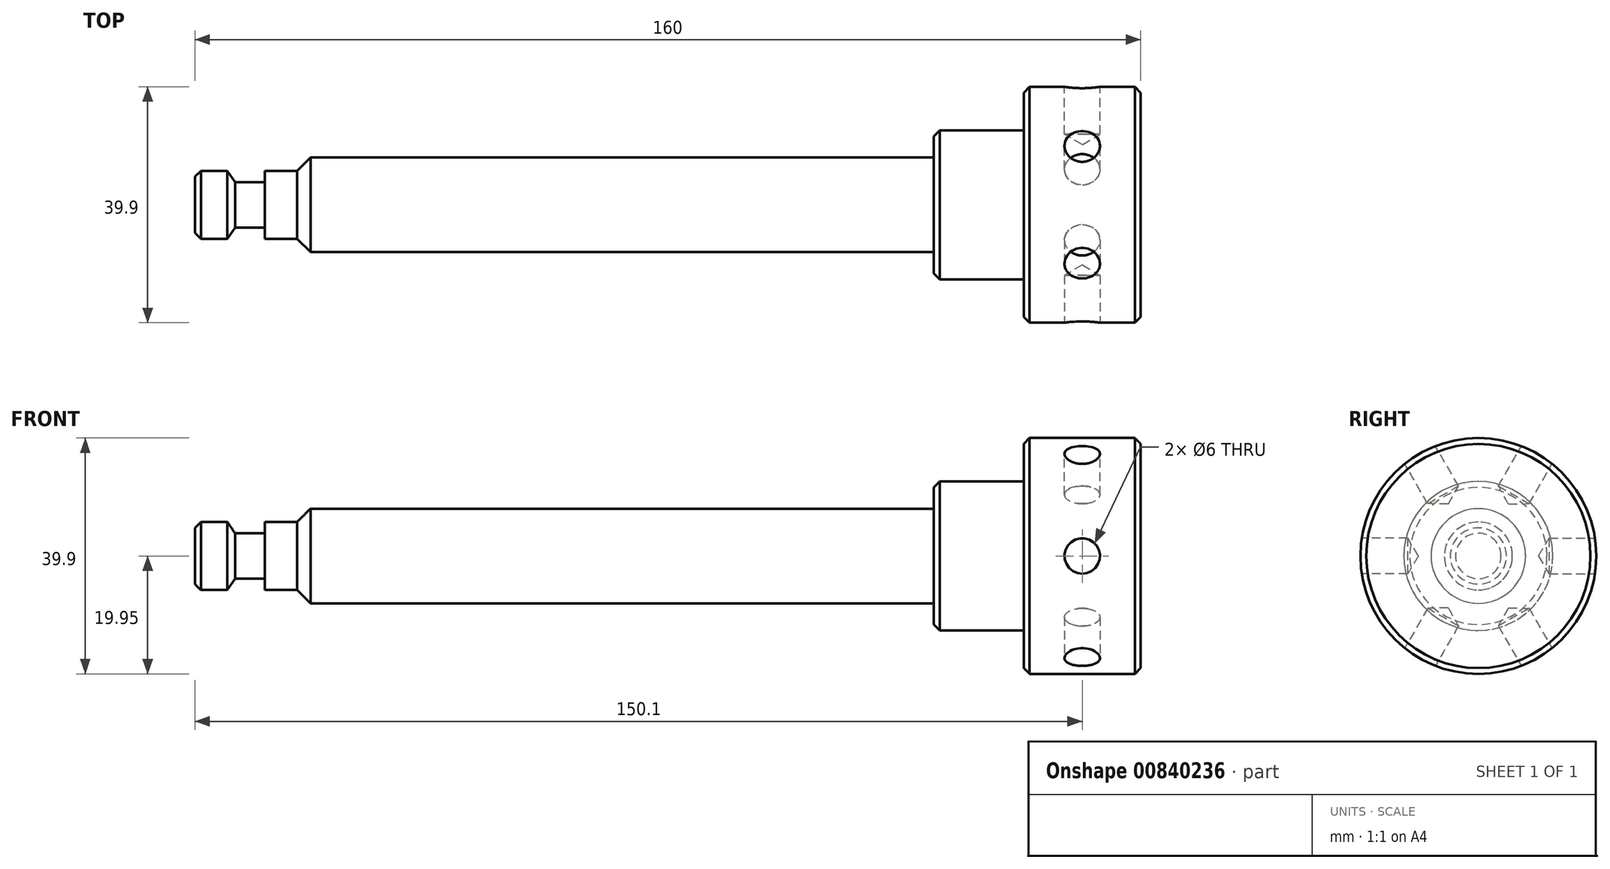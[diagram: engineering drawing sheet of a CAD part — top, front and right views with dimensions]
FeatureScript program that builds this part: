
annotation { "Feature Type Name" : "Feature", "Feature Type Description" : "" }
export const myFeature = defineFeature(function(context is Context, id is Id, definition is map)
    precondition{}
    {
        {
            var Q0;
            Q0=qCreatedBy(makeId("Top.planeOp"),FACE);
            var sketch = newSketch(context, id + "F0", { "sketchPlane" : qUnion([Q0])});
            skLineSegment(sketch, "E0", {"start": v(-0.14, 0) * mm, "end": v(-177.57, 0) * mm, "construction": true});
            skLineSegment(sketch, "E1", {"start": v(0, 0) * mm, "end": v(0, 19.95) * mm});
            skLineSegment(sketch, "E2", {"start": v(0, 19.95) * mm, "end": v(-19.8, 19.95) * mm});
            skLineSegment(sketch, "E3", {"start": v(-19.8, 19.95) * mm, "end": v(-19.8, 12.6) * mm});
            skLineSegment(sketch, "E4", {"start": v(-19.8, 12.6) * mm, "end": v(-35, 12.6) * mm});
            skLineSegment(sketch, "E5", {"start": v(-35, 12.6) * mm, "end": v(-35, 8) * mm});
            skLineSegment(sketch, "E6", {"start": v(-35, 8) * mm, "end": v(-142.7, 8) * mm});
            skLineSegment(sketch, "E7", {"start": v(-142.7, 8) * mm, "end": v(-142.7, 5.75) * mm});
            skLineSegment(sketch, "E8", {"start": v(-142.7, 5.75) * mm, "end": v(-148.2, 5.75) * mm});
            skLineSegment(sketch, "E9", {"start": v(-148.2, 5.75) * mm, "end": v(-148.2, 3.85) * mm});
            skLineSegment(sketch, "E10", {"start": v(-148.2, 3.85) * mm, "end": v(-153.2, 3.85) * mm});
            skLineSegment(sketch, "E11", {"start": v(-153.2, 3.85) * mm, "end": v(-154.5, 5.75) * mm});
            skLineSegment(sketch, "E12", {"start": v(-154.5, 5.75) * mm, "end": v(-160, 5.75) * mm});
            skLineSegment(sketch, "E13", {"start": v(-160, 5.75) * mm, "end": v(-160, 0) * mm});
            skLineSegment(sketch, "E14", {"start": v(-160, 0) * mm, "end": v(0, 0) * mm});
            skSolve(sketch);
        }
        {
            var Q0;
            Q0=makeQuery(id+"F0.imprint","IMPRINT",FACE,{"disambiguationData":[TD([[makeQuery(id+"F0.imprint","IMPRINT",EDGE,{"derivedFrom":sQuery(id+"F0.wireOp",EDGE,"E1")}),1.0]])]});
            var Q1;
            Q1=sQuery(id+"F0.wireOp",EDGE,"E14");
            revolve(context, id + "F1", {"entities" : qUnion([Q0]), "axis" : qUnion([Q1]), "revolveType" : RevolveType.FULL});
        }
        {
            var Q0;
            Q0=makeQuery(id+"F1.opRevolve","SWEPT_EDGE",EDGE,{"disambiguationData":[OSD([sQuery(id+"F0.wireOp",EDGE,"E12"),sQuery(id+"F0.wireOp",EDGE,"E13")])]});
            var Q1;
            Q1=makeQuery(id+"F1.opRevolve","SWEPT_EDGE",EDGE,{"disambiguationData":[OSD([sQuery(id+"F0.wireOp",EDGE,"E1"),sQuery(id+"F0.wireOp",EDGE,"E2")])]});
            var Q2;
            Q2=makeQuery(id+"F1.opRevolve","SWEPT_EDGE",EDGE,{"disambiguationData":[OSD([sQuery(id+"F0.wireOp",EDGE,"E4"),sQuery(id+"F0.wireOp",EDGE,"E5")])]});
            var Q3;
            Q3=makeQuery(id+"F1.opRevolve","SWEPT_EDGE",EDGE,{"disambiguationData":[OSD([sQuery(id+"F0.wireOp",EDGE,"E2"),sQuery(id+"F0.wireOp",EDGE,"E3")])]});
            chamfer(context, id + "F2", {"entities" : qUnion([Q0, Q1, Q2, Q3]), "width" : 1 * mm, "tangentPropagation" : true});
        }
        {
            var Q0;
            Q0=makeQuery(id+"F1.opRevolve","SWEPT_EDGE",EDGE,{"disambiguationData":[OSD([sQuery(id+"F0.wireOp",EDGE,"E6"),sQuery(id+"F0.wireOp",EDGE,"E7")])]});
            chamfer(context, id + "F3", {"entities" : qUnion([Q0]), "width" : 2.25 * mm, "tangentPropagation" : true});
        }
        {
            var Q0;
            Q0=makeQuery(id+"F1.opRevolve","SWEPT_FACE",FACE,{"disambiguationData":[OSD([sQuery(id+"F0.wireOp",EDGE,"E1")])]});
            var sketch = newSketch(context, id + "F4", { "sketchPlane" : qUnion([Q0])});
            skLineSegment(sketch, "E15", {"start": v(0, 0) * mm, "end": v(26.9, 0) * mm, "construction": true});
            skLineSegment(sketch, "E16", {"start": v(19.95, 12.37) * mm, "end": v(19.95, -12.53) * mm, "construction": true});
            skLineSegment(sketch, "E17.1.0", {"start": v(-0.74, 23.46) * mm, "end": v(20.82, 11.01) * mm, "construction": true});
            skLineSegment(sketch, "E17.1.1", {"start": v(0, 0) * mm, "end": v(13.45, 23.3) * mm, "construction": true});
            skLineSegment(sketch, "E17.2.0", {"start": v(-20.69, 11.1) * mm, "end": v(0.87, 23.54) * mm, "construction": true});
            skLineSegment(sketch, "E17.2.1", {"start": v(0, 0) * mm, "end": v(-13.45, 23.3) * mm, "construction": true});
            skLineSegment(sketch, "E17.3.0", {"start": v(-19.95, -12.37) * mm, "end": v(-19.95, 12.53) * mm, "construction": true});
            skLineSegment(sketch, "E17.3.1", {"start": v(0, 0) * mm, "end": v(-26.9, 0) * mm, "construction": true});
            skLineSegment(sketch, "E17.4.0", {"start": v(0.74, -23.46) * mm, "end": v(-20.82, -11.01) * mm, "construction": true});
            skLineSegment(sketch, "E17.4.1", {"start": v(0, 0) * mm, "end": v(-13.45, -23.3) * mm, "construction": true});
            skLineSegment(sketch, "E17.5.0", {"start": v(20.69, -11.1) * mm, "end": v(-0.87, -23.54) * mm, "construction": true});
            skLineSegment(sketch, "E17.5.1", {"start": v(0, 0) * mm, "end": v(13.45, -23.3) * mm, "construction": true});
            skPoint(sketch, "E17.center", {"position": v(0, 0) * mm});
            skSolve(sketch);
        }
        {
            var Q0;
            Q0=sQuery(id+"F4.wireOp",EDGE,"E16");
            cPlane(context, id + "F5", {"entities" : qUnion([Q0]), "cplaneType" : CPlaneType.LINE_ANGLE, "offset" : 25 * mm, "angle" : 90 * degree, "width" : 150 * mm, "height" : 150 * mm});
        }
        {
            var Q0;
            Q0=sQuery(id+"F4.wireOp",EDGE,"E17.1.0");
            cPlane(context, id + "F6", {"entities" : qUnion([Q0]), "cplaneType" : CPlaneType.LINE_ANGLE, "offset" : 25 * mm, "angle" : 0 * degree, "width" : 150 * mm, "height" : 150 * mm});
        }
        {
            var Q0;
            Q0=sQuery(id+"F4.wireOp",EDGE,"E17.2.0");
            cPlane(context, id + "F7", {"entities" : qUnion([Q0]), "cplaneType" : CPlaneType.LINE_ANGLE, "offset" : 25 * mm, "angle" : 0 * degree, "width" : 150 * mm, "height" : 150 * mm});
        }
        {
            var Q0;
            Q0=sQuery(id+"F4.wireOp",EDGE,"E17.3.0");
            cPlane(context, id + "F8", {"entities" : qUnion([Q0]), "cplaneType" : CPlaneType.LINE_ANGLE, "offset" : 25 * mm, "angle" : 90 * degree, "width" : 150 * mm, "height" : 150 * mm});
        }
        {
            var Q0;
            Q0=sQuery(id+"F4.wireOp",EDGE,"E17.4.0");
            cPlane(context, id + "F9", {"entities" : qUnion([Q0]), "cplaneType" : CPlaneType.LINE_ANGLE, "offset" : 25 * mm, "angle" : 0 * degree, "width" : 150 * mm, "height" : 150 * mm});
        }
        {
            var Q0;
            Q0=sQuery(id+"F4.wireOp",EDGE,"E17.5.0");
            cPlane(context, id + "F10", {"entities" : qUnion([Q0]), "cplaneType" : CPlaneType.LINE_ANGLE, "offset" : 25 * mm, "angle" : 0 * degree, "width" : 150 * mm, "height" : 150 * mm});
        }
        {
            var Q0;
            Q0=qCreatedBy(id+"F10.planeOp",FACE);
            var sketch = newSketch(context, id + "F11", { "sketchPlane" : qUnion([Q0])});
            skLineSegment(sketch, "E18", {"start": v(0, 0) * mm, "end": v(-24.04, 0) * mm, "construction": true});
            skPoint(sketch, "E19", {"position": v(-9.9, 0) * mm});
            skSolve(sketch);
        }
        {
            var Q0;
            Q0=qCreatedBy(id+"F9.planeOp",FACE);
            var sketch = newSketch(context, id + "F12", { "sketchPlane" : qUnion([Q0])});
            skLineSegment(sketch, "E20", {"start": v(0, 0) * mm, "end": v(-25.52, 0) * mm, "construction": true});
            skPoint(sketch, "E21", {"position": v(-9.9, 0) * mm});
            skSolve(sketch);
        }
        {
            var Q0;
            Q0=qCreatedBy(id+"F8.planeOp",FACE);
            var sketch = newSketch(context, id + "F13", { "sketchPlane" : qUnion([Q0])});
            skLineSegment(sketch, "E22", {"start": v(0, 0) * mm, "end": v(23.65, 0) * mm, "construction": true});
            skPoint(sketch, "E23", {"position": v(9.9, 0) * mm});
            skSolve(sketch);
        }
        {
            var Q0;
            Q0=qCreatedBy(id+"F7.planeOp",FACE);
            var sketch = newSketch(context, id + "F14", { "sketchPlane" : qUnion([Q0])});
            skLineSegment(sketch, "E24", {"start": v(0, 0) * mm, "end": v(-26.22, 0) * mm, "construction": true});
            skPoint(sketch, "E25", {"position": v(-9.9, 0) * mm});
            skSolve(sketch);
        }
        {
            var Q0;
            Q0=qCreatedBy(id+"F6.planeOp",FACE);
            var sketch = newSketch(context, id + "F15", { "sketchPlane" : qUnion([Q0])});
            skLineSegment(sketch, "E26", {"start": v(0, 0) * mm, "end": v(-33.74, 0) * mm, "construction": true});
            skPoint(sketch, "E27", {"position": v(-9.9, 0) * mm});
            skSolve(sketch);
        }
        {
            var Q0;
            Q0=qCreatedBy(id+"F5.planeOp",FACE);
            var sketch = newSketch(context, id + "F16", { "sketchPlane" : qUnion([Q0])});
            skLineSegment(sketch, "E28", {"start": v(0, 0) * mm, "end": v(19.8, 0) * mm, "construction": true});
            skPoint(sketch, "E29", {"position": v(9.9, 0) * mm});
            skSolve(sketch);
        }
        {
            var Q0;
            Q0=sQuery(id+"F13.wireOp",VERTEX,"E23");
            var Q1;
            Q1=makeQuery(id+"F1.opRevolve","SWEPT_BODY",BODY,{"disambiguationData":[OSD([sQuery(id+"F0.wireOp",EDGE,"E1"),sQuery(id+"F0.wireOp",EDGE,"E2"),sQuery(id+"F0.wireOp",EDGE,"E3"),sQuery(id+"F0.wireOp",EDGE,"E4"),sQuery(id+"F0.wireOp",EDGE,"E5"),sQuery(id+"F0.wireOp",EDGE,"E6"),sQuery(id+"F0.wireOp",EDGE,"E7"),sQuery(id+"F0.wireOp",EDGE,"E8"),sQuery(id+"F0.wireOp",EDGE,"E9"),sQuery(id+"F0.wireOp",EDGE,"E10"),sQuery(id+"F0.wireOp",EDGE,"E11"),sQuery(id+"F0.wireOp",EDGE,"E12"),sQuery(id+"F0.wireOp",EDGE,"E13"),sQuery(id+"F0.wireOp",EDGE,"E14")])]});
            hole(context, id + "F17", {"style" : HoleStyle.SIMPLE, "endStyle" : HoleEndStyle.BLIND, "oppositeDirection" : true, "holeDiameter" : 6 * mm, "holeDepth" : 8 * mm, "startFromSketch" : true, "locations" : qUnion([Q0]), "scope" : qUnion([Q1])});
        }
        {
            var Q0;
            Q0=sQuery(id+"F14.wireOp",VERTEX,"E25");
            var Q1;
            Q1=makeQuery(id+"F1.opRevolve","SWEPT_BODY",BODY,{"disambiguationData":[OSD([sQuery(id+"F0.wireOp",EDGE,"E1"),sQuery(id+"F0.wireOp",EDGE,"E2"),sQuery(id+"F0.wireOp",EDGE,"E3"),sQuery(id+"F0.wireOp",EDGE,"E4"),sQuery(id+"F0.wireOp",EDGE,"E5"),sQuery(id+"F0.wireOp",EDGE,"E6"),sQuery(id+"F0.wireOp",EDGE,"E7"),sQuery(id+"F0.wireOp",EDGE,"E8"),sQuery(id+"F0.wireOp",EDGE,"E9"),sQuery(id+"F0.wireOp",EDGE,"E10"),sQuery(id+"F0.wireOp",EDGE,"E11"),sQuery(id+"F0.wireOp",EDGE,"E12"),sQuery(id+"F0.wireOp",EDGE,"E13"),sQuery(id+"F0.wireOp",EDGE,"E14")])]});
            hole(context, id + "F18", {"style" : HoleStyle.SIMPLE, "endStyle" : HoleEndStyle.BLIND, "holeDiameter" : 6 * mm, "holeDepth" : 8 * mm, "startFromSketch" : true, "locations" : qUnion([Q0]), "scope" : qUnion([Q1])});
        }
        {
            var Q0;
            Q0=sQuery(id+"F15.wireOp",VERTEX,"E27");
            var Q1;
            Q1=makeQuery(id+"F1.opRevolve","SWEPT_BODY",BODY,{"disambiguationData":[OSD([sQuery(id+"F0.wireOp",EDGE,"E1"),sQuery(id+"F0.wireOp",EDGE,"E2"),sQuery(id+"F0.wireOp",EDGE,"E3"),sQuery(id+"F0.wireOp",EDGE,"E4"),sQuery(id+"F0.wireOp",EDGE,"E5"),sQuery(id+"F0.wireOp",EDGE,"E6"),sQuery(id+"F0.wireOp",EDGE,"E7"),sQuery(id+"F0.wireOp",EDGE,"E8"),sQuery(id+"F0.wireOp",EDGE,"E9"),sQuery(id+"F0.wireOp",EDGE,"E10"),sQuery(id+"F0.wireOp",EDGE,"E11"),sQuery(id+"F0.wireOp",EDGE,"E12"),sQuery(id+"F0.wireOp",EDGE,"E13"),sQuery(id+"F0.wireOp",EDGE,"E14")])]});
            hole(context, id + "F19", {"style" : HoleStyle.SIMPLE, "endStyle" : HoleEndStyle.BLIND, "holeDiameter" : 6 * mm, "holeDepth" : 8 * mm, "startFromSketch" : true, "locations" : qUnion([Q0]), "scope" : qUnion([Q1])});
        }
        {
            var Q0;
            Q0=sQuery(id+"F16.wireOp",VERTEX,"E29");
            var Q1;
            Q1=makeQuery(id+"F1.opRevolve","SWEPT_BODY",BODY,{"disambiguationData":[OSD([sQuery(id+"F0.wireOp",EDGE,"E1"),sQuery(id+"F0.wireOp",EDGE,"E2"),sQuery(id+"F0.wireOp",EDGE,"E3"),sQuery(id+"F0.wireOp",EDGE,"E4"),sQuery(id+"F0.wireOp",EDGE,"E5"),sQuery(id+"F0.wireOp",EDGE,"E6"),sQuery(id+"F0.wireOp",EDGE,"E7"),sQuery(id+"F0.wireOp",EDGE,"E8"),sQuery(id+"F0.wireOp",EDGE,"E9"),sQuery(id+"F0.wireOp",EDGE,"E10"),sQuery(id+"F0.wireOp",EDGE,"E11"),sQuery(id+"F0.wireOp",EDGE,"E12"),sQuery(id+"F0.wireOp",EDGE,"E13"),sQuery(id+"F0.wireOp",EDGE,"E14")])]});
            hole(context, id + "F20", {"style" : HoleStyle.SIMPLE, "endStyle" : HoleEndStyle.BLIND, "holeDiameter" : 6 * mm, "holeDepth" : 8 * mm, "startFromSketch" : true, "locations" : qUnion([Q0]), "scope" : qUnion([Q1])});
        }
        {
            var Q0;
            Q0=sQuery(id+"F11.wireOp",VERTEX,"E19");
            var Q1;
            Q1=makeQuery(id+"F1.opRevolve","SWEPT_BODY",BODY,{"disambiguationData":[OSD([sQuery(id+"F0.wireOp",EDGE,"E1"),sQuery(id+"F0.wireOp",EDGE,"E2"),sQuery(id+"F0.wireOp",EDGE,"E3"),sQuery(id+"F0.wireOp",EDGE,"E4"),sQuery(id+"F0.wireOp",EDGE,"E5"),sQuery(id+"F0.wireOp",EDGE,"E6"),sQuery(id+"F0.wireOp",EDGE,"E7"),sQuery(id+"F0.wireOp",EDGE,"E8"),sQuery(id+"F0.wireOp",EDGE,"E9"),sQuery(id+"F0.wireOp",EDGE,"E10"),sQuery(id+"F0.wireOp",EDGE,"E11"),sQuery(id+"F0.wireOp",EDGE,"E12"),sQuery(id+"F0.wireOp",EDGE,"E13"),sQuery(id+"F0.wireOp",EDGE,"E14")])]});
            hole(context, id + "F21", {"style" : HoleStyle.SIMPLE, "endStyle" : HoleEndStyle.BLIND, "holeDiameter" : 6 * mm, "holeDepth" : 8 * mm, "startFromSketch" : true, "locations" : qUnion([Q0]), "scope" : qUnion([Q1])});
        }
        {
            var Q0;
            Q0=sQuery(id+"F12.wireOp",VERTEX,"E21");
            var Q1;
            Q1=makeQuery(id+"F1.opRevolve","SWEPT_BODY",BODY,{"disambiguationData":[OSD([sQuery(id+"F0.wireOp",EDGE,"E1"),sQuery(id+"F0.wireOp",EDGE,"E2"),sQuery(id+"F0.wireOp",EDGE,"E3"),sQuery(id+"F0.wireOp",EDGE,"E4"),sQuery(id+"F0.wireOp",EDGE,"E5"),sQuery(id+"F0.wireOp",EDGE,"E6"),sQuery(id+"F0.wireOp",EDGE,"E7"),sQuery(id+"F0.wireOp",EDGE,"E8"),sQuery(id+"F0.wireOp",EDGE,"E9"),sQuery(id+"F0.wireOp",EDGE,"E10"),sQuery(id+"F0.wireOp",EDGE,"E11"),sQuery(id+"F0.wireOp",EDGE,"E12"),sQuery(id+"F0.wireOp",EDGE,"E13"),sQuery(id+"F0.wireOp",EDGE,"E14")])]});
            hole(context, id + "F22", {"style" : HoleStyle.SIMPLE, "endStyle" : HoleEndStyle.BLIND, "holeDiameter" : 6 * mm, "holeDepth" : 8 * mm, "startFromSketch" : true, "locations" : qUnion([Q0]), "scope" : qUnion([Q1])});
        }
    });
